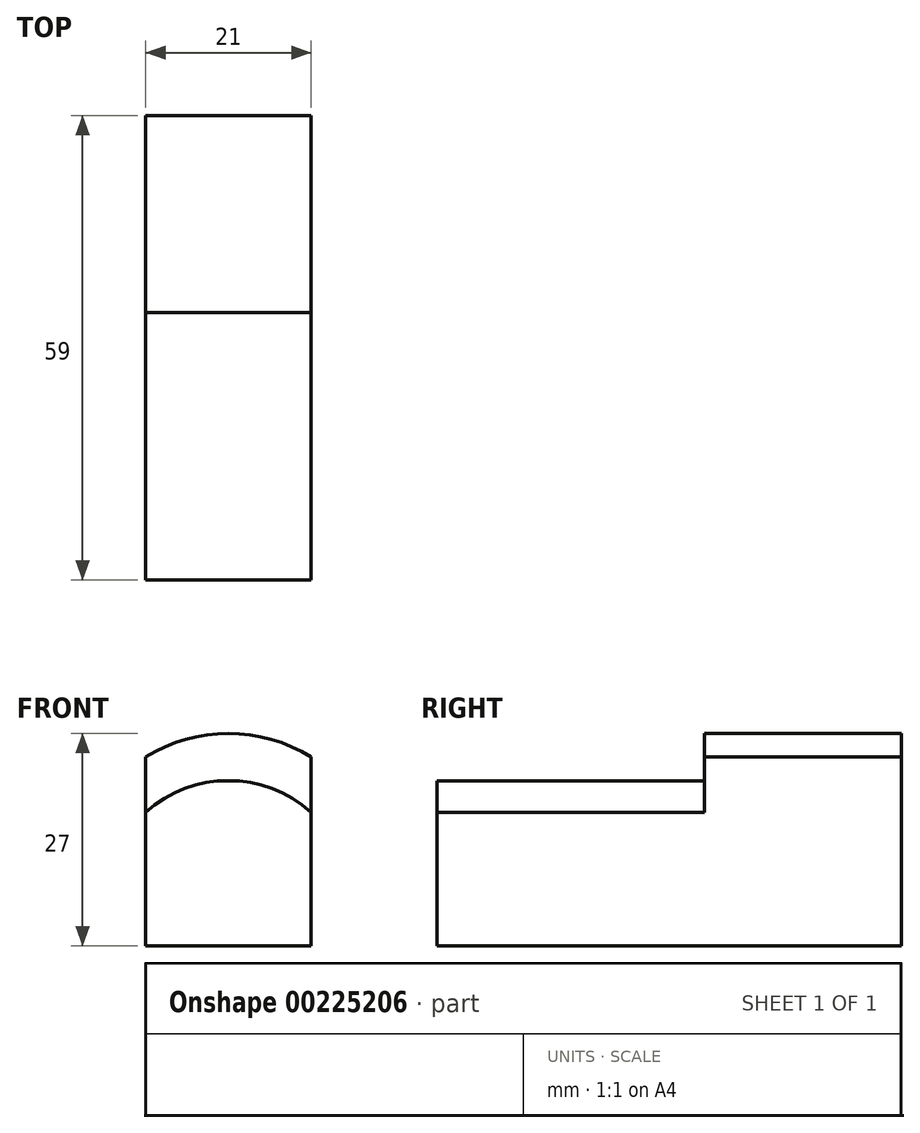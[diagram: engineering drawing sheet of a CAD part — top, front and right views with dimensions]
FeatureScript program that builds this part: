
annotation { "Feature Type Name" : "Feature", "Feature Type Description" : "" }
export const myFeature = defineFeature(function(context is Context, id is Id, definition is map)
    precondition{}
    {
        {
            var Q0;
            Q0=qCreatedBy(makeId("Front.planeOp"),FACE);
            var sketch = newSketch(context, id + "F0", { "sketchPlane" : qUnion([Q0])});
            skLineSegment(sketch, "E0.bottom", {"start": v(10.5, 0) * mm, "end": v(-10.5, 0) * mm});
            skLineSegment(sketch, "E0.top", {"start": v(10.5, 17) * mm, "end": v(-10.5, 17) * mm, "construction": true});
            skLineSegment(sketch, "E0.left", {"start": v(10.5, 0) * mm, "end": v(10.5, 17) * mm});
            skLineSegment(sketch, "E0.right", {"start": v(-10.5, 0) * mm, "end": v(-10.5, 17) * mm});
            skPoint(sketch, "E0.middle", {"position": v(0, 8.5) * mm});
            skArc(sketch, "E1", {"start": v(10.5, 17) * mm, "mid": v(0, 21) * mm, "end": v(-10.5, 17) * mm});
            skLineSegment(sketch, "E2.top", {"start": v(10.5, 24) * mm, "end": v(-10.5, 24) * mm, "construction": true});
            skLineSegment(sketch, "E2.left", {"start": v(10.5, 17) * mm, "end": v(10.5, 24) * mm});
            skLineSegment(sketch, "E2.right", {"start": v(-10.5, 17) * mm, "end": v(-10.5, 24) * mm});
            skArc(sketch, "E3", {"start": v(10.5, 24) * mm, "mid": v(0, 27) * mm, "end": v(-10.5, 24) * mm});
            skSolve(sketch);
        }
        {
            var Q0;
            Q0=makeQuery(id+"F0.imprint","IMPRINT",FACE,{"disambiguationData":[TD([[makeQuery(id+"F0.imprint","IMPRINT",EDGE,{"derivedFrom":sQuery(id+"F0.wireOp",EDGE,"E0.bottom")}),-1.0]])]});
            extrude(context, id + "F1", {"entities" : qUnion([Q0]), "depth" : 59 * mm});
        }
        {
            var Q0;
            Q0=makeQuery(id+"F0.imprint","IMPRINT",FACE,{"disambiguationData":[TD([[makeQuery(id+"F0.imprint","IMPRINT",EDGE,{"derivedFrom":sQuery(id+"F0.wireOp",EDGE,"E1")}),-1.0]])]});
            extrude(context, id + "F2", {"entities" : qUnion([Q0]), "operationType" : NewBodyOperationType.ADD, "depth" : 25 * mm});
        }
    });
